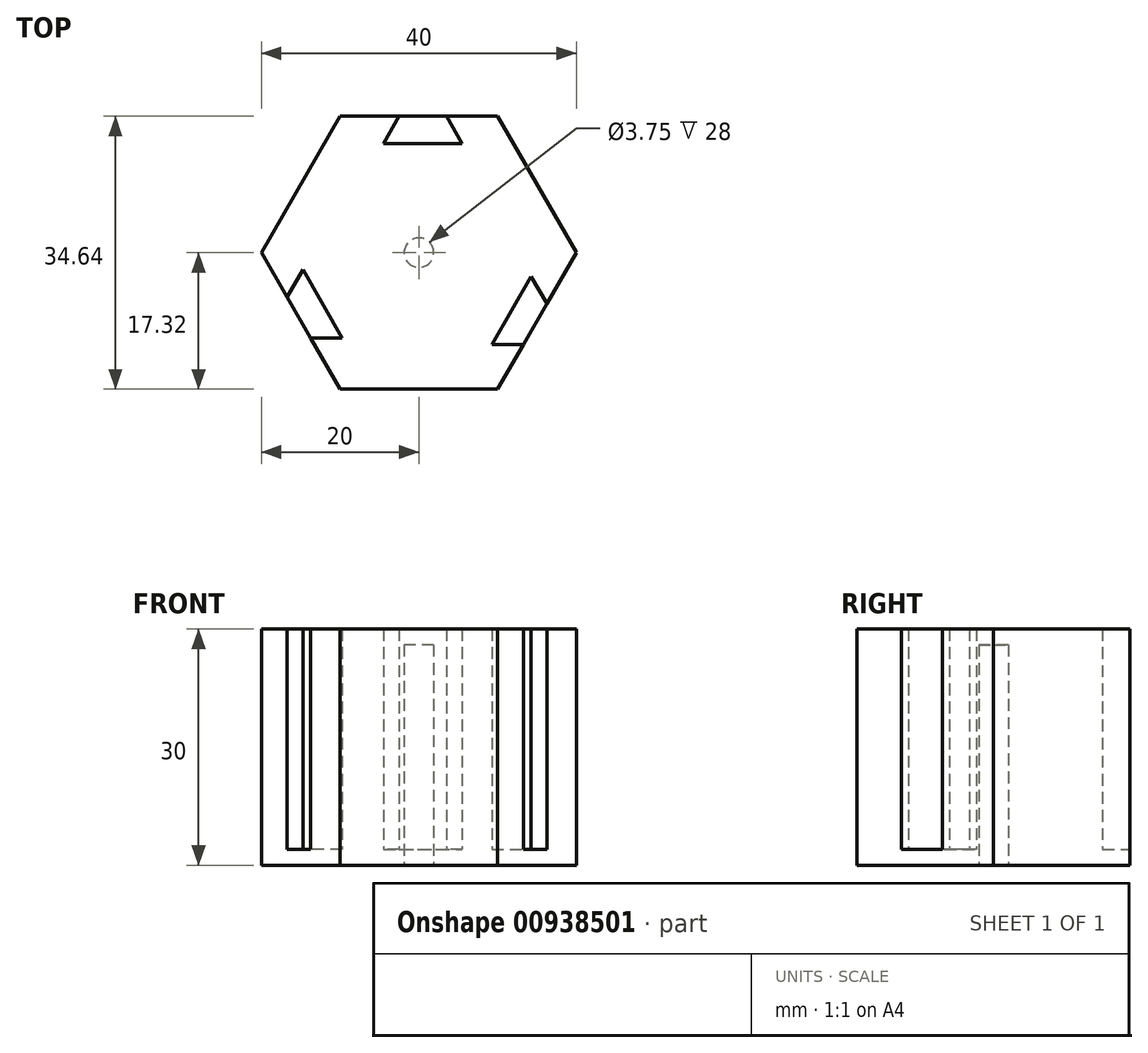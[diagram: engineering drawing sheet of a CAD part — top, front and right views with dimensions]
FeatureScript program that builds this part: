
annotation { "Feature Type Name" : "Feature", "Feature Type Description" : "" }
export const myFeature = defineFeature(function(context is Context, id is Id, definition is map)
    precondition{}
    {
        {
            var Q0;
            Q0=qCreatedBy(makeId("Top.planeOp"),FACE);
            var sketch = newSketch(context, id + "F0", { "sketchPlane" : qUnion([Q0])});
            skCircle(sketch, "E0.cCircle", {"center": v(0, 0) * mm, "radius": 20 * mm, "construction": true});
            skLineSegment(sketch, "E0.0", {"start": v(10, -17.32) * mm, "end": v(-10, -17.32) * mm});
            skLineSegment(sketch, "E0.1", {"start": v(-10, -17.32) * mm, "end": v(-20, 0) * mm});
            skLineSegment(sketch, "E0.2", {"start": v(-20, 0) * mm, "end": v(-10, 17.32) * mm});
            skLineSegment(sketch, "E0.3", {"start": v(-10, 17.32) * mm, "end": v(10, 17.32) * mm});
            skLineSegment(sketch, "E0.4", {"start": v(10, 17.32) * mm, "end": v(20, 0) * mm});
            skLineSegment(sketch, "E0.5", {"start": v(20, 0) * mm, "end": v(10, -17.32) * mm});
            skLineSegment(sketch, "E1", {"start": v(-4.5, 13.86) * mm, "end": v(5.5, 13.86) * mm});
            skLineSegment(sketch, "E2", {"start": v(5.5, 13.86) * mm, "end": v(3.5, 17.32) * mm});
            skLineSegment(sketch, "E3", {"start": v(3.5, 17.32) * mm, "end": v(-2.5, 17.32) * mm});
            skLineSegment(sketch, "E4", {"start": v(-2.5, 17.32) * mm, "end": v(-4.5, 13.86) * mm});
            skLineSegment(sketch, "E5.1.0", {"start": v(-9.75, -10.83) * mm, "end": v(-14.75, -2.17) * mm});
            skLineSegment(sketch, "E5.1.1", {"start": v(-13.75, -10.83) * mm, "end": v(-9.75, -10.83) * mm});
            skLineSegment(sketch, "E5.1.2", {"start": v(-14.75, -2.17) * mm, "end": v(-16.75, -5.63) * mm});
            skLineSegment(sketch, "E5.2.0", {"start": v(14.25, -3.03) * mm, "end": v(9.25, -11.7) * mm});
            skLineSegment(sketch, "E5.2.1", {"start": v(16.25, -6.5) * mm, "end": v(14.25, -3.03) * mm});
            skLineSegment(sketch, "E5.2.2", {"start": v(9.25, -11.7) * mm, "end": v(13.25, -11.7) * mm});
            skCircle(sketch, "E6", {"center": v(0, 0) * mm, "radius": 1.88 * mm});
            skSolve(sketch);
        }
        {
            var Q0;
            {var subQ1=sQuery(id+"F0.wireOp",EDGE,"E0.0");Q0=makeQuery(id+"F0.imprint","IMPRINT",FACE,{"disambiguationData":[TD([[makeQuery(id+"F0.imprint","IMPRINT",EDGE,{"derivedFrom":subQ1}),-1.0]])]});}
            extrude(context, id + "F1", {"entities" : qUnion([Q0]), "depth" : 30 * mm, "offsetDistance" : 25 * mm});
        }
        {
            var Q0;
            Q0=makeQuery(id+"F0.imprint","IMPRINT",FACE,{"disambiguationData":[TD([[makeQuery(id+"F0.imprint","IMPRINT",EDGE,{"derivedFrom":sQuery(id+"F0.wireOp",EDGE,"E5.1.0")}),1.0]])]});
            var Q1;
            Q1=makeQuery(id+"F0.imprint","IMPRINT",FACE,{"disambiguationData":[TD([[makeQuery(id+"F0.imprint","IMPRINT",EDGE,{"derivedFrom":sQuery(id+"F0.wireOp",EDGE,"E5.2.0")}),1.0]])]});
            var Q2;
            Q2=makeQuery(id+"F0.imprint","IMPRINT",FACE,{"disambiguationData":[TD([[makeQuery(id+"F0.imprint","IMPRINT",EDGE,{"derivedFrom":sQuery(id+"F0.wireOp",EDGE,"E1")}),1.0]])]});
            extrude(context, id + "F2", {"entities" : qUnion([Q0, Q1, Q2]), "operationType" : NewBodyOperationType.ADD, "depth" : 2 * mm, "offsetDistance" : 25 * mm});
        }
        {
            var Q0;
            Q0=makeQuery(id+"F0.imprint","IMPRINT",FACE,{"disambiguationData":[TD([[makeQuery(id+"F0.imprint","IMPRINT",EDGE,{"derivedFrom":sQuery(id+"F0.wireOp",EDGE,"E6")}),1.0]])]});
            extrude(context, id + "F3", {"entities" : qUnion([Q0]), "operationType" : NewBodyOperationType.ADD, "depth" : 30 * mm, "offsetDistance" : 25 * mm, "hasSecondDirection" : true, "secondDirectionOppositeDirection" : false, "secondDirectionDepth" : 28 * mm});
        }
    });
